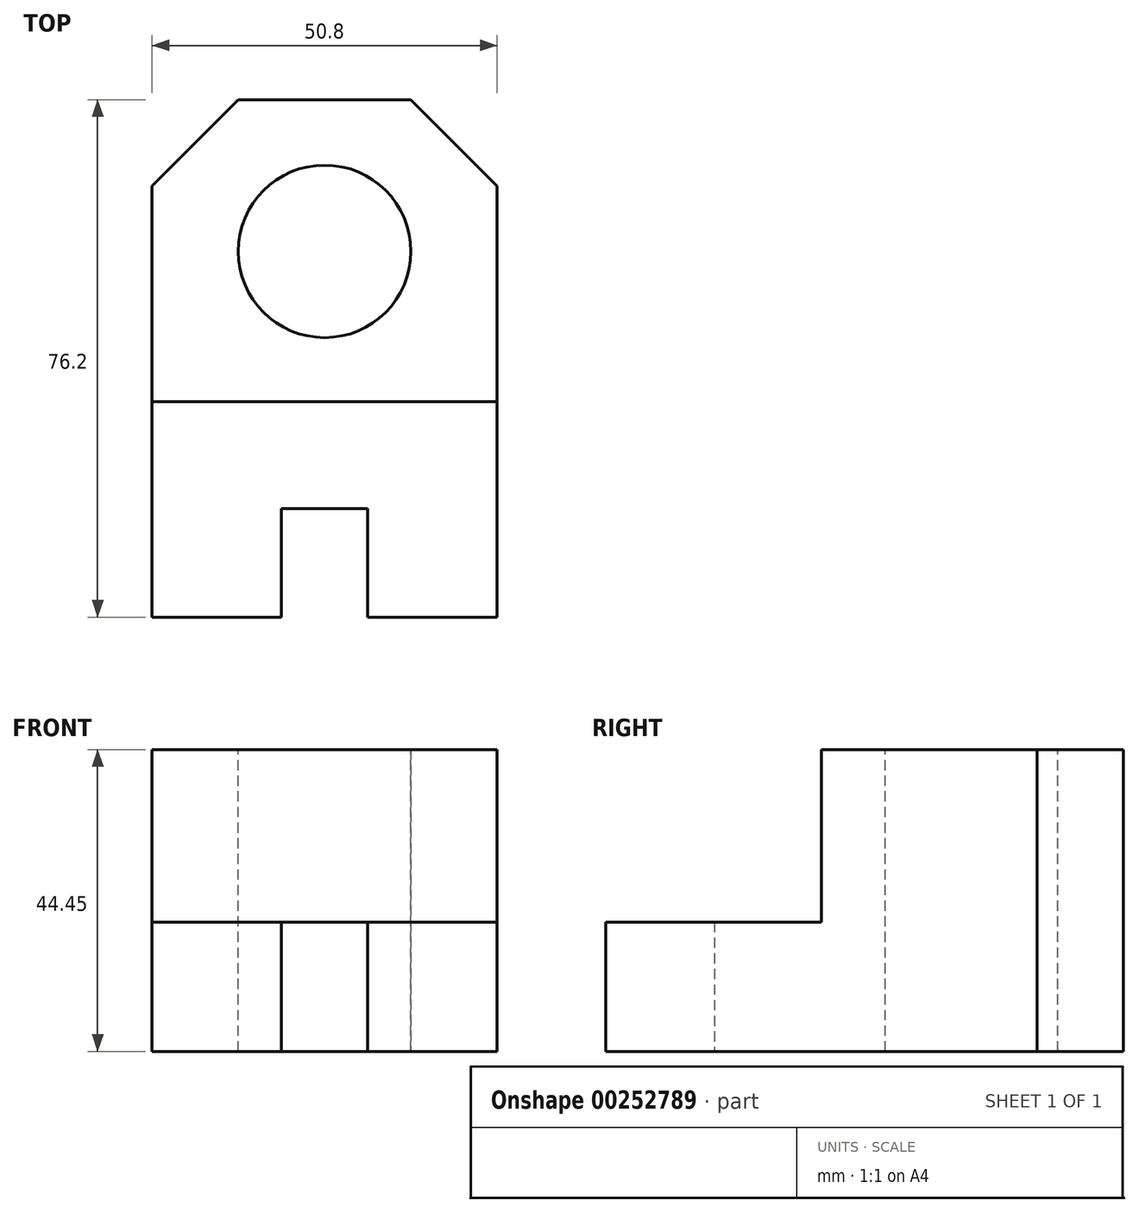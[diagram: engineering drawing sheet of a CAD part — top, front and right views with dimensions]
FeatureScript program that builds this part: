
annotation { "Feature Type Name" : "Feature", "Feature Type Description" : "" }
export const myFeature = defineFeature(function(context is Context, id is Id, definition is map)
    precondition{}
    {
        {
            var Q0;
            Q0=qCreatedBy(makeId("Top.planeOp"),FACE);
            var sketch = newSketch(context, id + "F0", { "sketchPlane" : qUnion([Q0])});
            skLineSegment(sketch, "E0", {"start": v(-6.96, 0) * mm, "end": v(-6.96, 16) * mm});
            skLineSegment(sketch, "E1", {"start": v(-6.96, 16) * mm, "end": v(5.74, 16) * mm});
            skLineSegment(sketch, "E2", {"start": v(5.74, 16) * mm, "end": v(5.74, 0) * mm});
            skLineSegment(sketch, "E3", {"start": v(5.74, 0) * mm, "end": v(24.8, 0) * mm});
            skLineSegment(sketch, "E4", {"start": v(-6.96, 0) * mm, "end": v(-26, 0) * mm});
            skLineSegment(sketch, "E5", {"start": v(-26, 0) * mm, "end": v(-26, 31.75) * mm});
            skLineSegment(sketch, "E6", {"start": v(24.8, 0) * mm, "end": v(24.8, 31.75) * mm});
            skLineSegment(sketch, "E7", {"start": v(-26, 31.75) * mm, "end": v(24.8, 31.75) * mm});
            skLineSegment(sketch, "E8", {"start": v(-26, 31.75) * mm, "end": v(-26, 76.2) * mm});
            skLineSegment(sketch, "E9", {"start": v(24.8, 31.75) * mm, "end": v(24.8, 76.2) * mm});
            skLineSegment(sketch, "E10", {"start": v(-26, 76.2) * mm, "end": v(24.8, 76.2) * mm});
            skSolve(sketch);
        }
        {
            var Q0;
            Q0=makeQuery(id+"F0.imprint","IMPRINT",FACE,{"disambiguationData":[TD([[makeQuery(id+"F0.imprint","IMPRINT",EDGE,{"derivedFrom":sQuery(id+"F0.wireOp",EDGE,"E0")}),1.0]])]});
            extrude(context, id + "F1", {"entities" : qUnion([Q0]), "depth" : 19.05 * mm});
        }
        {
            var Q0;
            Q0=makeQuery(id+"F0.imprint","IMPRINT",FACE,{"disambiguationData":[TD([[makeQuery(id+"F0.imprint","IMPRINT",EDGE,{"derivedFrom":sQuery(id+"F0.wireOp",EDGE,"E7")}),1.0]])]});
            extrude(context, id + "F2", {"entities" : qUnion([Q0]), "operationType" : NewBodyOperationType.ADD, "depth" : 44.45 * mm});
        }
        {
            var Q0;
            Q0=makeQuery(id+"F2.opExtrude","SWEPT_EDGE",EDGE,{"disambiguationData":[OSD([sQuery(id+"F0.wireOp",EDGE,"E9"),sQuery(id+"F0.wireOp",EDGE,"E10")])]});
            var Q1;
            Q1=makeQuery(id+"F2.opExtrude","SWEPT_EDGE",EDGE,{"disambiguationData":[OSD([sQuery(id+"F0.wireOp",EDGE,"E8"),sQuery(id+"F0.wireOp",EDGE,"E10")])]});
            chamfer(context, id + "F3", {"entities" : qUnion([Q0, Q1]), "width" : 12.7 * mm, "tangentPropagation" : true});
        }
        {
            var Q0;
            Q0=makeQuery(id+"F2.opExtrude","CAP_FACE",FACE,{"disambiguationData":[OSD([sQuery(id+"F0.wireOp",EDGE,"E7"),sQuery(id+"F0.wireOp",EDGE,"E8"),sQuery(id+"F0.wireOp",EDGE,"E9"),sQuery(id+"F0.wireOp",EDGE,"E10")])],"isStart":false});
            var sketch = newSketch(context, id + "F4", { "sketchPlane" : qUnion([Q0])});
            skLineSegment(sketch, "E11", {"start": v(-0.6, 76.2) * mm, "end": v(-0.6, 53.85) * mm});
            skSolve(sketch);
        }
        {
            var Q0;
            Q0=sQuery(id+"F4.wireOp",VERTEX,"E11.end");
            var Q1;
            Q1=makeQuery(id+"F1.opExtrude","SWEPT_BODY",BODY,{"disambiguationData":[OSD([sQuery(id+"F0.wireOp",EDGE,"E0"),sQuery(id+"F0.wireOp",EDGE,"E1"),sQuery(id+"F0.wireOp",EDGE,"E2"),sQuery(id+"F0.wireOp",EDGE,"E3"),sQuery(id+"F0.wireOp",EDGE,"E4"),sQuery(id+"F0.wireOp",EDGE,"E5"),sQuery(id+"F0.wireOp",EDGE,"E6"),sQuery(id+"F0.wireOp",EDGE,"E7")])]});
            hole(context, id + "F5", {"style" : HoleStyle.SIMPLE, "endStyle" : HoleEndStyle.THROUGH, "holeDiameter" : 25.4 * mm, "tappedDepth" : 12.7 * mm, "tapClearance" : 3, "locations" : qUnion([Q0]), "scope" : qUnion([Q1])});
        }
    });
